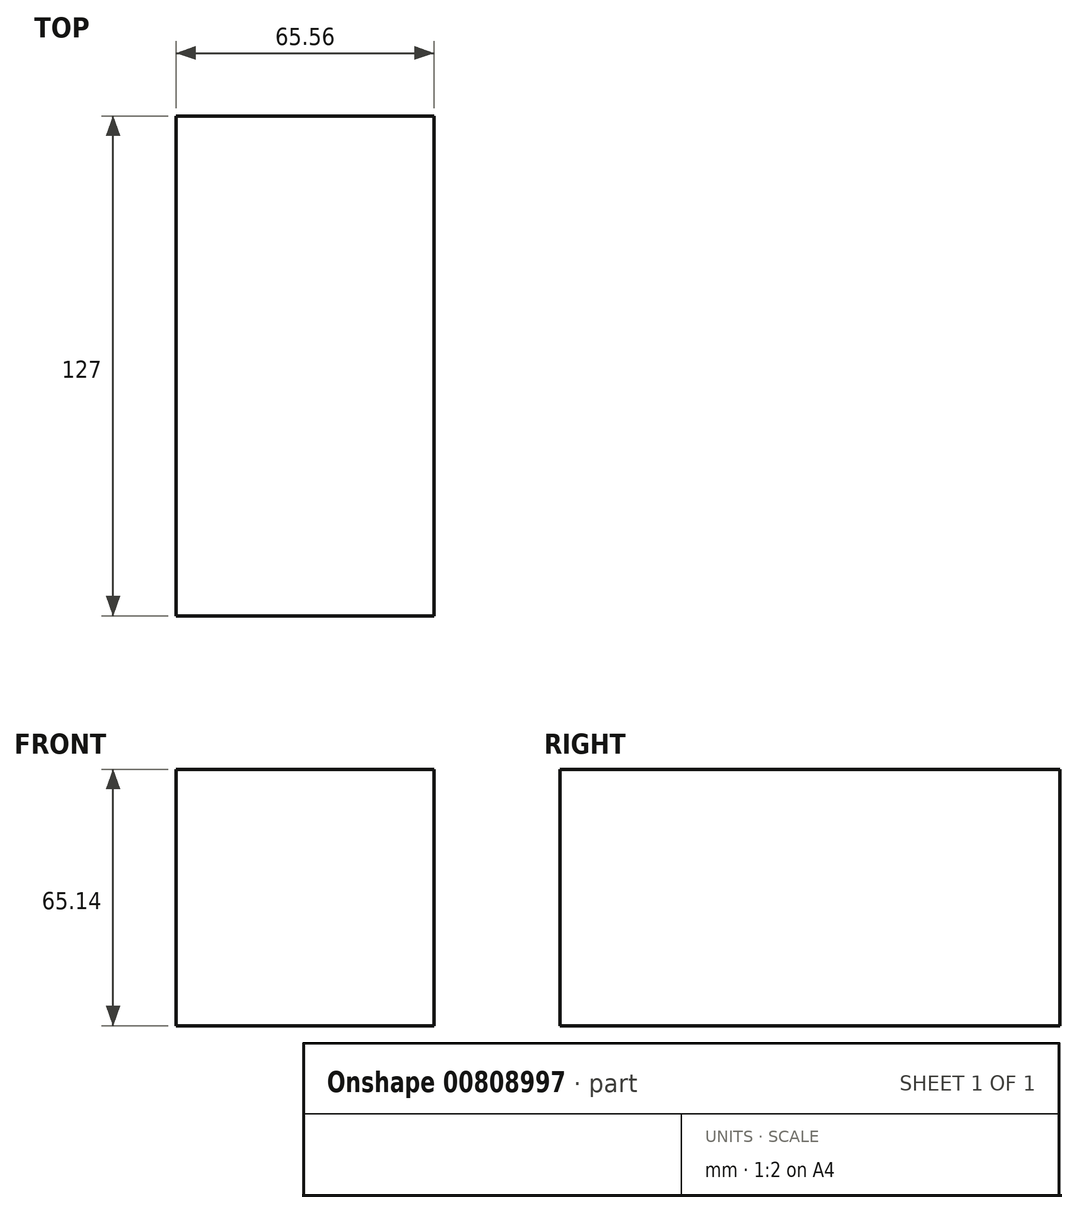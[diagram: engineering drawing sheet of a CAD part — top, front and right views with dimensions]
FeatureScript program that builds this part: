
annotation { "Feature Type Name" : "Feature", "Feature Type Description" : "" }
export const myFeature = defineFeature(function(context is Context, id is Id, definition is map)
    precondition{}
    {
        {
            var Q0;
            Q0=qCreatedBy(makeId("Front.planeOp"),FACE);
            var sketch = newSketch(context, id + "F0", { "sketchPlane" : qUnion([Q0])});
            skLineSegment(sketch, "E0.bottom", {"start": v(0, 0) * mm, "end": v(65.56, 0) * mm});
            skLineSegment(sketch, "E0.top", {"start": v(0, -65.14) * mm, "end": v(65.56, -65.14) * mm});
            skLineSegment(sketch, "E0.left", {"start": v(0, 0) * mm, "end": v(0, -65.14) * mm});
            skLineSegment(sketch, "E0.right", {"start": v(65.56, 0) * mm, "end": v(65.56, -65.14) * mm});
            skSolve(sketch);
        }
        {
            var Q0;
            Q0=makeQuery(id+"F0.imprint","IMPRINT",FACE,{"disambiguationData":[TD([[makeQuery(id+"F0.imprint","IMPRINT",EDGE,{"derivedFrom":sQuery(id+"F0.wireOp",EDGE,"E0.bottom")}),-1.0]])]});
            var sketch = newSketch(context, id + "F1", { "sketchPlane" : qUnion([Q0])});
            skSolve(sketch);
        }
        {
            var Q0;
            Q0=makeQuery(id+"F1.imprint","IMPRINT",FACE,{"disambiguationData":[TD([[makeQuery(id+"F1.imprint","IMPRINT",EDGE,{"derivedFrom":makeQuery(id+"F0.imprint","IMPRINT",EDGE,{"derivedFrom":sQuery(id+"F0.wireOp",EDGE,"E0.bottom")})}),-1.0]])]});
            extrude(context, id + "F2", {"entities" : qUnion([Q0]), "depth" : 127 * mm, "offsetDistance" : 25.4 * mm});
        }
    });
